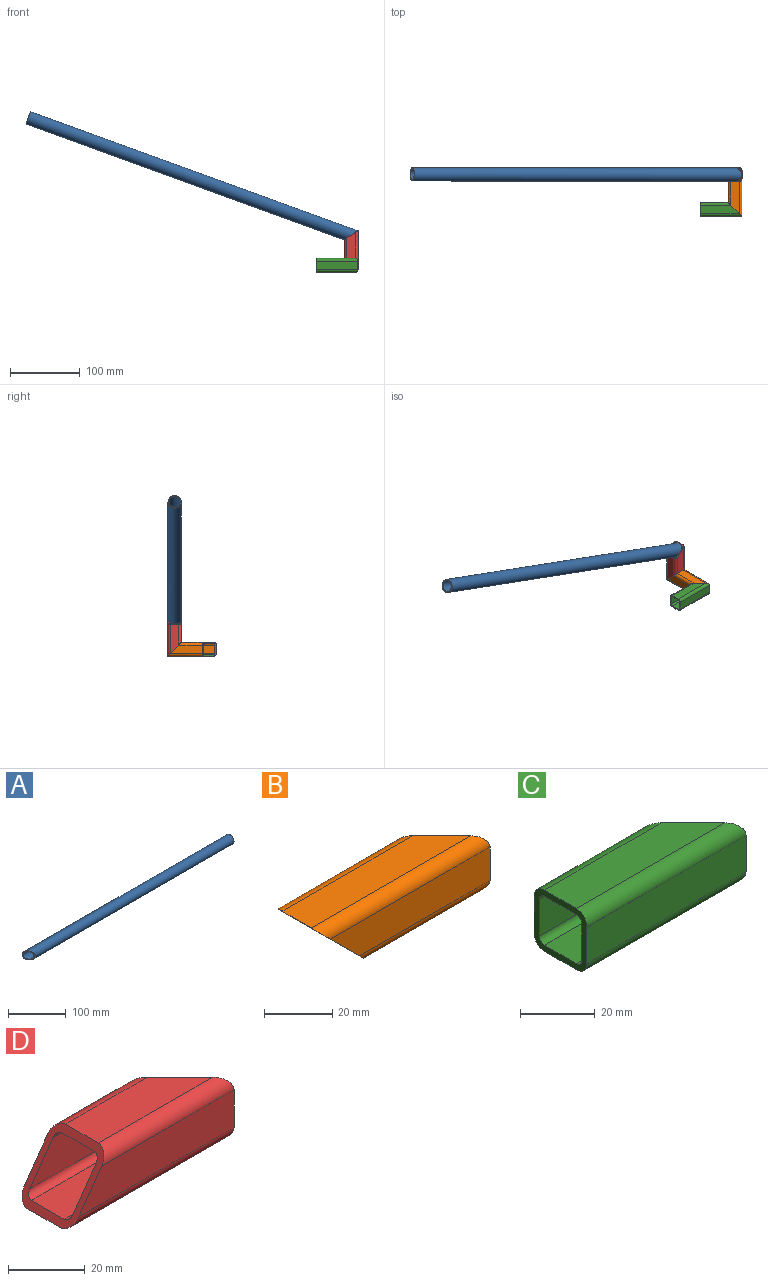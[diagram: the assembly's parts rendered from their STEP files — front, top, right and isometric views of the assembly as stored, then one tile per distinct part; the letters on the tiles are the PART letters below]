
ASSEMBLY  parts=4 mates=3
PART A: 4 faces, bbox 500x19x19 mm
  f0: cylinder r=7.9mm len=498.88mm, axis (-1,0,0), area 24488.4mm2, adj f2,f3
  f1: cylinder r=9.5mm len=500mm, axis (-1,0,0), area 29448.1mm2, adj f2,f3
  f2: plane 19x19mm, normal (1,0,0), area 87.5mm2, adj f0,f1
  f3: plane 19x19mm, normal (-0.82,-0.57,0), area 106.8mm2, adj f0,f1
PART B: 18 faces, bbox 70x20x20 mm
  f0: plane 66x12mm, normal (0,-1,0), area 720mm2, adj f9,f12,f16,f17
  f1: plane 64x12mm, normal (0,0,-1), area 696mm2, adj f2,f8,f16,f17
  f2: cylinder r=2mm len=52mm, axis (1,0,0), area 157.1mm2, adj f1,f3,f16,f17
  f3: plane 48x12mm, normal (0,-1,0), area 504mm2, adj f2,f4,f16,f17
  f4: cylinder r=2mm len=38mm, axis (1,0,0), area 111.4mm2, adj f3,f5,f16,f17
  f5: plane 48x12mm, normal (0,0,1), area 504mm2, adj f4,f6,f16,f17
  f6: cylinder r=2mm len=52mm, axis (1,0,0), area 157.1mm2, adj f5,f7,f16,f17
  f7: plane 64x12mm, normal (0,1,0), area 696mm2, adj f6,f8,f16,f17
  f8: cylinder r=2mm len=66mm, axis (1,0,0), area 202.8mm2, adj f1,f7,f16,f17
  f9: cylinder r=4mm len=54mm, axis (1,0,0), area 314.1mm2, adj f0,f15,f16,f17
  f10: cylinder r=4mm len=38mm, axis (1,0,0), area 206.7mm2, adj f13,f15,f16,f17
  f11: cylinder r=4mm len=54mm, axis (1,0,0), area 314.1mm2, adj f13,f14,f16,f17
  f12: cylinder r=4mm len=70mm, axis (1,0,0), area 421.5mm2, adj f0,f14,f16,f17
  f13: plane 46x12mm, normal (0,1,0), area 480mm2, adj f10,f11,f16,f17
  f14: plane 66x12mm, normal (0,0,1), area 720mm2, adj f11,f12,f16,f17
  f15: plane 46x12mm, normal (0,0,-1), area 480mm2, adj f9,f10,f16,f17
  f16: plane 20x20mm, normal (0.71,0.71,0), area 189.1mm2, adj f0,f1,f2,f3,f4,f5,f6,f7
  f17: plane 20x20mm, normal (-0.71,0,-0.71), area 189.1mm2, adj f0,f1,f2,f3,f4,f5,f6,f7
PART C: 18 faces, bbox 60x20x20 mm
  f0: plane 56x12mm, normal (0,0,1), area 600mm2, adj f12,f13,f14,f17
  f1: plane 56x12mm, normal (0,0,-1), area 600mm2, adj f2,f8,f14,f17
  f2: cylinder r=2mm len=44mm, axis (1,0,0), area 134.2mm2, adj f1,f3,f14,f17
  f3: plane 42x12mm, normal (0,-1,0), area 504mm2, adj f2,f4,f14,f17
  f4: cylinder r=2mm len=44mm, axis (1,0,0), area 134.2mm2, adj f3,f5,f14,f17
  f5: plane 56x12mm, normal (0,0,1), area 600mm2, adj f4,f6,f14,f17
  f6: cylinder r=2mm len=58mm, axis (1,0,0), area 179.9mm2, adj f5,f7,f14,f17
  f7: plane 58x12mm, normal (0,1,0), area 696mm2, adj f6,f8,f14,f17
  f8: cylinder r=2mm len=58mm, axis (1,0,0), area 179.9mm2, adj f1,f7,f14,f17
  f9: cylinder r=4mm len=60mm, axis (1,0,0), area 367.8mm2, adj f10,f14,f15,f17
  f10: plane 56x12mm, normal (0,0,-1), area 600mm2, adj f9,f11,f14,f17
  f11: cylinder r=4mm len=44mm, axis (1,0,0), area 260.4mm2, adj f10,f14,f16,f17
  f12: cylinder r=4mm len=44mm, axis (1,0,0), area 260.4mm2, adj f0,f14,f16,f17
  f13: cylinder r=4mm len=60mm, axis (1,0,0), area 367.8mm2, adj f0,f14,f15,f17
  f14: plane 20x20mm, normal (-1,0,0), area 133.7mm2, adj f0,f1,f2,f3,f4,f5,f6,f7
  f15: plane 60x12mm, normal (0,-1,0), area 720mm2, adj f9,f13,f14,f17
  f16: plane 40x12mm, normal (0,1,0), area 480mm2, adj f11,f12,f14,f17
  f17: plane 20x20mm, normal (0.71,0.71,0), area 189.1mm2, adj f0,f1,f2,f3,f4,f5,f6,f7
PART D: 18 faces, bbox 60x20x20 mm
  f0: plane 37.2x12mm, normal (0,1,0), area 396mm2, adj f10,f11,f16,f17
  f1: plane 43.4x12mm, normal (0,0,-1), area 448.8mm2, adj f2,f8,f16,f17
  f2: cylinder r=2mm len=32.8mm, axis (1,0,0), area 96.2mm2, adj f1,f3,f16,f17
  f3: plane 39.2x12mm, normal (0,-1,0), area 420mm2, adj f2,f4,f16,f17
  f4: cylinder r=2mm len=42.6mm, axis (1,0,0), area 128.2mm2, adj f3,f5,f16,f17
  f5: plane 54.6x12mm, normal (0,0,1), area 583.2mm2, adj f4,f6,f16,f17
  f6: cylinder r=2mm len=56.6mm, axis (1,0,0), area 173.9mm2, adj f5,f7,f16,f17
  f7: plane 55.2x12mm, normal (0,1,0), area 612mm2, adj f6,f8,f16,f17
  f8: cylinder r=2mm len=46.8mm, axis (1,0,0), area 141.9mm2, adj f1,f7,f16,f17
  f9: cylinder r=4mm len=60mm, axis (1,0,0), area 361.4mm2, adj f13,f15,f16,f17
  f10: cylinder r=4mm len=44mm, axis (1,0,0), area 254mm2, adj f0,f15,f16,f17
  f11: cylinder r=4mm len=32.8mm, axis (1,0,0), area 178.8mm2, adj f0,f14,f16,f17
  f12: cylinder r=4mm len=48.8mm, axis (1,0,0), area 286.2mm2, adj f13,f14,f16,f17
  f13: plane 57.2x12mm, normal (0,-1,0), area 636mm2, adj f9,f12,f16,f17
  f14: plane 42x12mm, normal (0,0,1), area 432mm2, adj f11,f12,f16,f17
  f15: plane 56x12mm, normal (0,0,-1), area 600mm2, adj f9,f10,f16,f17
  f16: plane 20x20mm, normal (0.71,0.71,0), area 189.1mm2, adj f0,f1,f2,f3,f4,f5,f6,f7
  f17: plane 20x20mm, normal (-0.82,0,0.57), area 163.2mm2, adj f0,f1,f2,f3,f4,f5,f6,f7
PLACE A rot(axis=(-0.12,-0.7,-0.7),165.9deg) t=(-713.75,-72.3,262.24)mm
PLACE B rot(axis=(0.71,-0.71,0),180deg) t=(-250.15,-62.3,50.51)mm
PLACE C t=(-300.15,-122.3,50.51)mm fixed
PLACE D rot(axis=(-0.71,0,0.71),180deg) t=(-250.15,-72.3,100.51)mm
MATE fastened C.f17 <-> B.f16  axis (0.71,0.71,0) through (-250.15,-122.3,50.51)mm
MATE fastened D.f16 <-> B.f17  axis (0,-0.71,-0.71) through (-250.15,-72.3,50.51)mm
MATE fastened A.f3 <-> D.f17  axis (0.57,0,-0.82) through (-250.15,-72.3,93.51)mm
